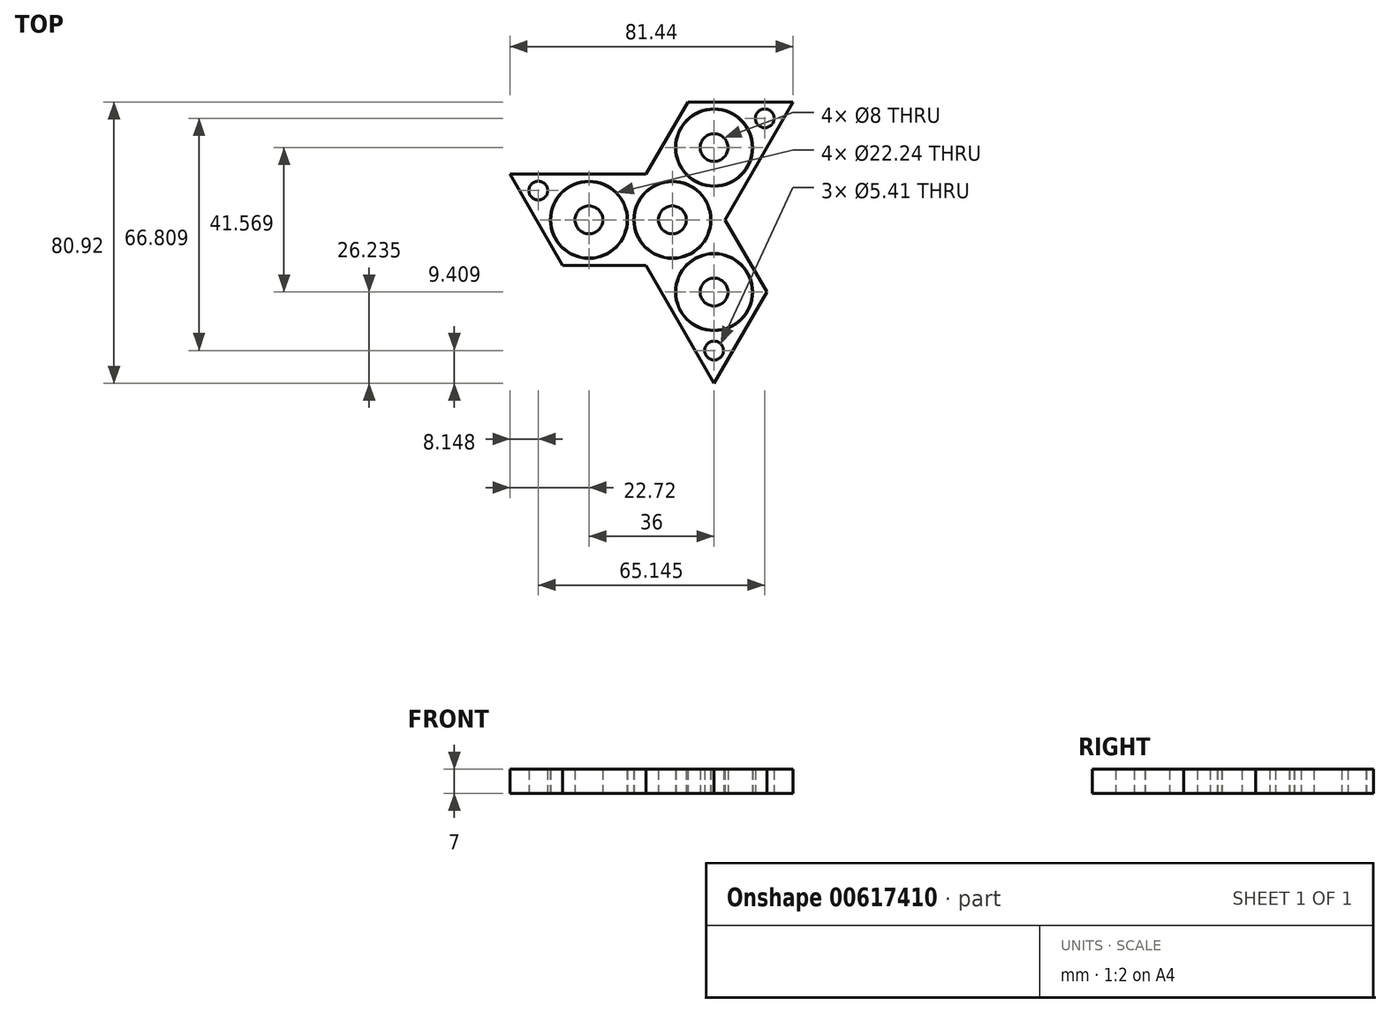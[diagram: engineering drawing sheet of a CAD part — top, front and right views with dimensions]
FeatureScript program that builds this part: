
annotation { "Feature Type Name" : "Feature", "Feature Type Description" : "" }
export const myFeature = defineFeature(function(context is Context, id is Id, definition is map)
    precondition{}
    {
        {
            var Q0;
            Q0=qCreatedBy(makeId("Top.planeOp"),FACE);
            var sketch = newSketch(context, id + "F0", { "sketchPlane" : qUnion([Q0])});
            skCircle(sketch, "E0", {"center": v(0, 0) * mm, "radius": 11 * mm});
            skCircle(sketch, "E1", {"center": v(0, 0) * mm, "radius": 4 * mm});
            skSolve(sketch);
        }
        {
            var Q0;
            Q0=makeQuery(id+"F0.imprint","IMPRINT",FACE,{"disambiguationData":[TD([[makeQuery(id+"F0.imprint","IMPRINT",EDGE,{"derivedFrom":sQuery(id+"F0.wireOp",EDGE,"E0")}),1.0]])]});
            extrude(context, id + "F1", {"entities" : qUnion([Q0]), "endBound" : BoundingType.SYMMETRIC, "depth" : 7 * mm, "offsetDistance" : 25 * mm});
        }
        {
            var Q0;
            Q0=qCreatedBy(makeId("Top.planeOp"),FACE);
            var sketch = newSketch(context, id + "F2", { "sketchPlane" : qUnion([Q0])});
            skCircle(sketch, "E2", {"center": v(-24, 0) * mm, "radius": 11 * mm});
            skCircle(sketch, "E3", {"center": v(-24, 0) * mm, "radius": 4 * mm});
            skCircle(sketch, "E4.1.0", {"center": v(12, -20.78) * mm, "radius": 4 * mm});
            skCircle(sketch, "E4.1.1", {"center": v(12, -20.78) * mm, "radius": 11 * mm});
            skCircle(sketch, "E4.2.0", {"center": v(12, 20.78) * mm, "radius": 4 * mm});
            skCircle(sketch, "E4.2.1", {"center": v(12, 20.78) * mm, "radius": 11 * mm});
            skPoint(sketch, "E4.center", {"position": v(0, 0) * mm});
            skCircle(sketch, "E5.0", {"center": v(-24, 0) * mm, "radius": 11.12 * mm});
            skCircle(sketch, "E6.0", {"center": v(0, 0) * mm, "radius": 11.12 * mm});
            skCircle(sketch, "E7.1.0", {"center": v(12, -20.78) * mm, "radius": 11.12 * mm});
            skCircle(sketch, "E7.2.0", {"center": v(12, 20.78) * mm, "radius": 11.12 * mm});
            skCircle(sketch, "E8.0", {"center": v(0, 0) * mm, "radius": 13.12 * mm});
            skLineSegment(sketch, "E9", {"start": v(0, 13.12) * mm, "end": v(-46.72, 13.12) * mm});
            skLineSegment(sketch, "E10", {"start": v(-46.72, 13.12) * mm, "end": v(-31.57, -13.12) * mm});
            skLineSegment(sketch, "E11", {"start": v(-31.57, -13.12) * mm, "end": v(-6.12, -13.12) * mm});
            skLineSegment(sketch, "E12.1.0", {"start": v(-11.36, -6.56) * mm, "end": v(12, -47.02) * mm});
            skLineSegment(sketch, "E12.1.1", {"start": v(12, -47.02) * mm, "end": v(27.15, -20.78) * mm});
            skLineSegment(sketch, "E12.1.2", {"start": v(27.15, -20.78) * mm, "end": v(14.42, 1.26) * mm});
            skLineSegment(sketch, "E12.2.0", {"start": v(11.36, -6.56) * mm, "end": v(34.72, 33.9) * mm});
            skLineSegment(sketch, "E12.2.1", {"start": v(34.72, 33.9) * mm, "end": v(4.43, 33.9) * mm});
            skLineSegment(sketch, "E12.2.2", {"start": v(4.43, 33.9) * mm, "end": v(-8.3, 11.86) * mm});
            skCircle(sketch, "E13", {"center": v(-38.57, 8.41) * mm, "radius": 2.7 * mm});
            skCircle(sketch, "E14.1.0", {"center": v(12, -37.61) * mm, "radius": 2.7 * mm});
            skCircle(sketch, "E14.2.0", {"center": v(26.57, 29.2) * mm, "radius": 2.7 * mm});
            skSolve(sketch);
        }
        {
            var Q0;
            Q0=makeQuery(id+"F2.imprint","IMPRINT",FACE,{"disambiguationData":[TD([[makeQuery(id+"F2.imprint","IMPRINT",EDGE,{"derivedFrom":sQuery(id+"F2.wireOp",EDGE,"E2")}),1.0]])]});
            var Q1;
            Q1=makeQuery(id+"F2.imprint","IMPRINT",FACE,{"disambiguationData":[TD([[makeQuery(id+"F2.imprint","IMPRINT",EDGE,{"derivedFrom":sQuery(id+"F2.wireOp",EDGE,"E4.2.0")}),-1.0]])]});
            var Q2;
            Q2=makeQuery(id+"F2.imprint","IMPRINT",FACE,{"disambiguationData":[TD([[makeQuery(id+"F2.imprint","IMPRINT",EDGE,{"derivedFrom":sQuery(id+"F2.wireOp",EDGE,"E4.1.0")}),-1.0]])]});
            var Q3;
            Q3=makeQuery(id+"F2.imprint","IMPRINT",FACE,{"disambiguationData":[TD([[makeQuery(id+"F2.imprint","IMPRINT",EDGE,{"derivedFrom":sQuery(id+"F2.wireOp",EDGE,"E5.0")}),-1.0]])]});
            var Q4;
            Q4=makeQuery(id+"F2.imprint","IMPRINT",FACE,{"disambiguationData":[TD([[makeQuery(id+"F2.imprint","IMPRINT",EDGE,{"derivedFrom":sQuery(id+"F2.wireOp",EDGE,"E7.1.0")}),-1.0]])]});
            var Q5;
            Q5=makeQuery(id+"F2.imprint","IMPRINT",FACE,{"disambiguationData":[TD([[makeQuery(id+"F2.imprint","IMPRINT",EDGE,{"derivedFrom":sQuery(id+"F2.wireOp",EDGE,"E7.2.0")}),-1.0]])]});
            var Q6;
            Q6=makeQuery(id+"F2.imprint","IMPRINT",FACE,{"disambiguationData":[TD([[makeQuery(id+"F2.imprint","IMPRINT",EDGE,{"derivedFrom":sQuery(id+"F2.wireOp",EDGE,"E6.0")}),-1.0]])]});
            var Q7;
            Q7=makeQuery(id+"F2.imprint","IMPRINT",FACE,{"disambiguationData":[TD([[makeQuery(id+"F2.imprint","IMPRINT",EDGE,{"derivedFrom":sQuery(id+"F2.wireOp",EDGE,"E3")}),-1.0]])]});
            var Q8;
            {var subQ0=sQuery(id+"F2.wireOp",EDGE,"E8.0");var subQ1=sQuery(id+"F2.wireOp",EDGE,"E4.1.1");var subQ2=makeQuery(id+"F2.imprint","INTERSECT",VERTEX,{"disambiguationData":[OD(0.0)],"derivedFrom":[subQ1,subQ0]});Q8=makeQuery(id+"F2.imprint","IMPRINT",FACE,{"disambiguationData":[TD([[makeQuery(id+"F2.imprint","IMPRINT",EDGE,{"disambiguationData":[TD([[subQ2,1.0]])],"derivedFrom":subQ1}),1.0]])]});}
            var Q9;
            {var subQ0=sQuery(id+"F2.wireOp",EDGE,"E8.0");var subQ1=sQuery(id+"F2.wireOp",EDGE,"E4.2.1");var subQ2=makeQuery(id+"F2.imprint","INTERSECT",VERTEX,{"disambiguationData":[OD(0.0)],"derivedFrom":[subQ1,subQ0]});Q9=makeQuery(id+"F2.imprint","IMPRINT",FACE,{"disambiguationData":[TD([[makeQuery(id+"F2.imprint","IMPRINT",EDGE,{"disambiguationData":[TD([[subQ2,1.0]])],"derivedFrom":subQ1}),1.0]])]});}
            extrude(context, id + "F3", {"entities" : qUnion([Q0, Q1, Q2, Q3, Q4, Q5, Q6, Q7, Q8, Q9]), "endBound" : BoundingType.SYMMETRIC, "depth" : 7 * mm, "offsetDistance" : 25 * mm});
        }
    });
